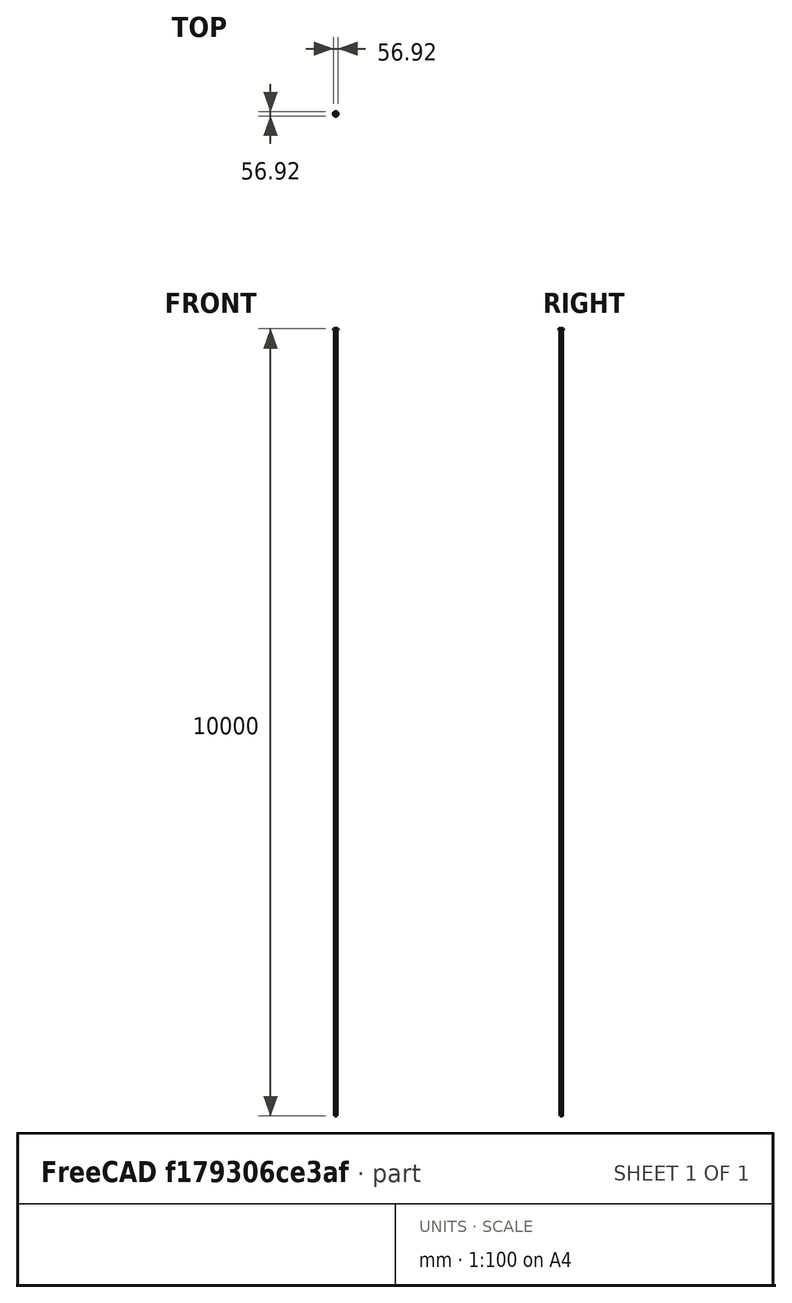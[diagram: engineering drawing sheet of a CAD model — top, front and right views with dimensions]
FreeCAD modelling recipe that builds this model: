
FCSTD DOCUMENT  (FreeCAD 0.16R)
Label: ST-DTsleeve
License: All rights reserved
LicenseURL: http://en.wikipedia.org/wiki/All_rights_reserved
objects: Part::Cylinder×2, Sketcher::SketchObject×2, PartDesign::Pocket×2, Part::Cut×1, Mesh::Feature×1
note: 9 computed .brp shape members not serialized (recipe doc carries the construction recipe); baked Part::Feature solids carry a one-line shape summary decoded from their .brp

FEATURE [Part::Cylinder] Cylinder
  Angle = 360
  Height = 49
  Placement = pos=(0,0,8.5) rot=(0,0,1;0rad)
  Radius = 16.3
FEATURE [Part::Cylinder] Cylinder001
  Angle = 360
  Height = 97
  Placement = pos=(-16,0,-2) rot=(0,1,0;1.09083rad)
  Radius = 15
FEATURE [Part::Cut] Cut
  Base = -> Cylinder
  Tool = -> Cylinder001
FEATURE [Sketcher::SketchObject] Sketch
  Placement = pos=(0,0,57.5) rot=(0,0,1;0rad)
  Support = -> Cut [Face5]
  sketch-geometry (1):
    g0: Circle CenterX=0 CenterY=0 CenterZ=0 NormalX=0 NormalY=0 NormalZ=1 Radius=14.6
  constraints (2):
    c: Coincident(g0,g-1)
    c: Radius(g0) = 14.6
FEATURE [PartDesign::Pocket] Pocket
  Length = 5
  Sketch = -> Sketch
  Type = 1
FEATURE [Sketcher::SketchObject] Sketch001
  Placement = pos=(0,0,57.5) rot=(0,0,1;0rad)
  Support = -> Pocket [Face5]
  sketch-geometry (1):
    g0: Circle CenterX=0 CenterY=0 CenterZ=0 NormalX=0 NormalY=0 NormalZ=1 Radius=28.4599
  constraints (1):
    c: Coincident(g0,g-1)
FEATURE [PartDesign::Pocket] Pocket001
  Length = 17
  Sketch = -> Sketch001
  Type = 0
FEATURE [Mesh::Feature] Mesh  label="Pocket001 (Meshed)"
